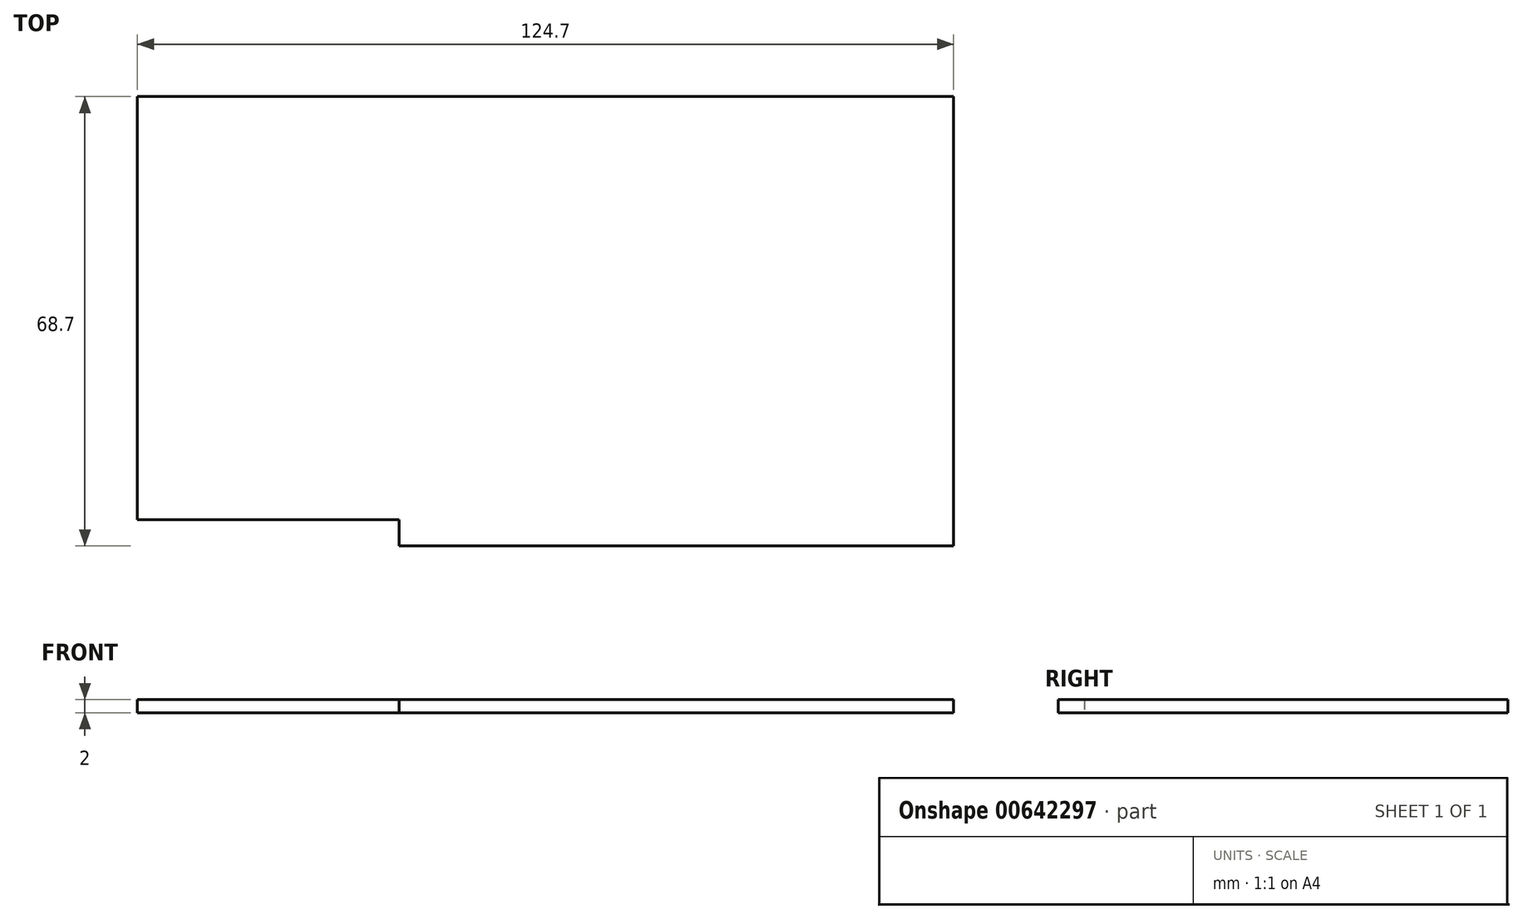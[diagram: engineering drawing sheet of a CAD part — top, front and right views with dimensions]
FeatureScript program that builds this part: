
annotation { "Feature Type Name" : "Feature", "Feature Type Description" : "" }
export const myFeature = defineFeature(function(context is Context, id is Id, definition is map)
    precondition{}
    {
        {
            var Q0;
            Q0=qCreatedBy(makeId("Top.planeOp"),FACE);
            var sketch = newSketch(context, id + "F0", { "sketchPlane" : qUnion([Q0])});
            skLineSegment(sketch, "E0.bottom", {"start": v(-32.92, -8.68) * mm, "end": v(92.08, -8.68) * mm});
            skLineSegment(sketch, "E0.top", {"start": v(-32.92, 60.32) * mm, "end": v(92.08, 60.32) * mm});
            skLineSegment(sketch, "E0.right", {"start": v(92.08, -8.68) * mm, "end": v(92.08, 60.32) * mm});
            skLineSegment(sketch, "E1", {"start": v(-32.92, -4.68) * mm, "end": v(7.08, -4.68) * mm});
            skLineSegment(sketch, "E2", {"start": v(7.08, -4.68) * mm, "end": v(7.08, -8.68) * mm});
            skLineSegment(sketch, "E3", {"start": v(-32.92, -4.68) * mm, "end": v(-32.92, 60.32) * mm});
            skLineSegment(sketch, "E4.bottom", {"start": v(91.93, 60.17) * mm, "end": v(7.23, 60.17) * mm});
            skLineSegment(sketch, "E4.top", {"start": v(91.93, -8.53) * mm, "end": v(7.23, -8.53) * mm});
            skLineSegment(sketch, "E4.left", {"start": v(91.93, 60.17) * mm, "end": v(91.93, -8.53) * mm});
            skLineSegment(sketch, "E4.right", {"start": v(7.23, 60.17) * mm, "end": v(7.23, -8.53) * mm});
            skLineSegment(sketch, "E5.bottom", {"start": v(7.23, 60.17) * mm, "end": v(-32.77, 60.17) * mm});
            skLineSegment(sketch, "E5.top", {"start": v(7.23, -4.53) * mm, "end": v(-32.77, -4.53) * mm});
            skLineSegment(sketch, "E5.left", {"start": v(7.23, 60.17) * mm, "end": v(7.23, -4.53) * mm});
            skLineSegment(sketch, "E5.right", {"start": v(-32.77, 60.17) * mm, "end": v(-32.77, -4.53) * mm});
            skSolve(sketch);
        }
        {
            var Q0;
            {var subQ0=sQuery(id+"F0.wireOp",EDGE,"E5.bottom");Q0=makeQuery(id+"F0.imprint","IMPRINT",FACE,{"disambiguationData":[TD([[makeQuery(id+"F0.imprint","IMPRINT",EDGE,{"derivedFrom":subQ0}),1.0]])]});}
            var Q1;
            {var subQ1=sQuery(id+"F0.wireOp",EDGE,"E4.bottom");Q1=makeQuery(id+"F0.imprint","IMPRINT",FACE,{"disambiguationData":[TD([[makeQuery(id+"F0.imprint","IMPRINT",EDGE,{"derivedFrom":subQ1}),1.0]])]});}
            extrude(context, id + "F1", {"entities" : qUnion([Q0, Q1]), "depth" : 2 * mm, "offsetDistance" : 25 * mm});
        }
    });
